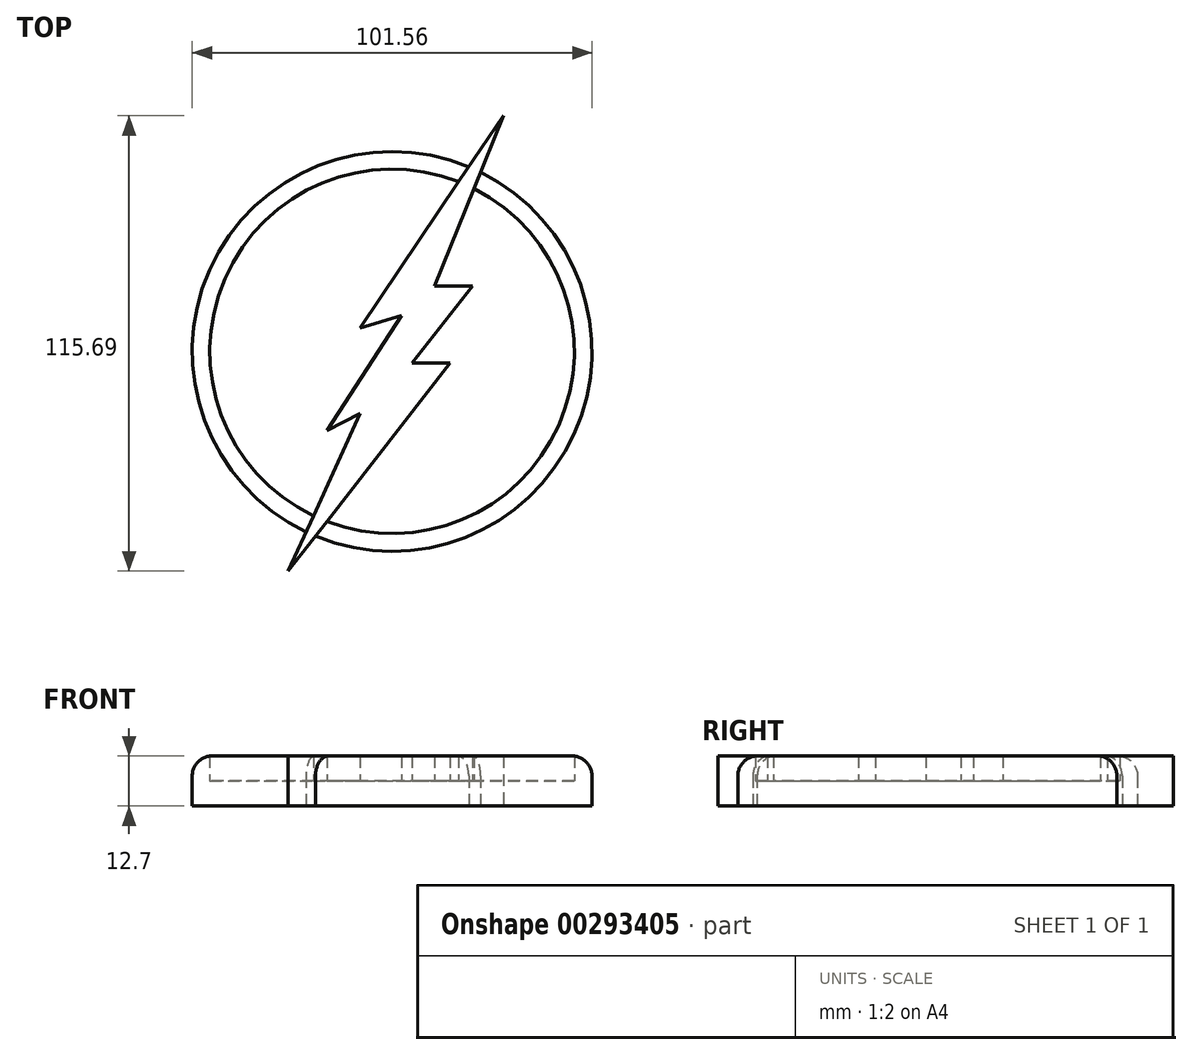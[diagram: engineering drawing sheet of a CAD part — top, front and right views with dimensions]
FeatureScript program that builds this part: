
annotation { "Feature Type Name" : "Feature", "Feature Type Description" : "" }
export const myFeature = defineFeature(function(context is Context, id is Id, definition is map)
    precondition{}
    {
        {
            var Q0;
            Q0=qCreatedBy(makeId("Top.planeOp"),FACE);
            var sketch = newSketch(context, id + "F0", { "sketchPlane" : qUnion([Q0])});
            skCircle(sketch, "E0", {"center": v(0, 0) * mm, "radius": 50.78 * mm});
            skCircle(sketch, "E1", {"center": v(0, 0) * mm, "radius": 46.3 * mm});
            skSolve(sketch);
        }
        {
            var Q0;
            Q0=makeQuery(id+"F0.imprint","IMPRINT",FACE,{"disambiguationData":[TD([[makeQuery(id+"F0.imprint","IMPRINT",EDGE,{"derivedFrom":sQuery(id+"F0.wireOp",EDGE,"E1")}),1.0]])]});
            extrude(context, id + "F1", {"entities" : qUnion([Q0]), "depth" : 6.35 * mm});
        }
        {
            var Q0;
            Q0=qSketchRegion(id+"F0",true);
            extrude(context, id + "F2", {"entities" : qUnion([Q0]), "operationType" : NewBodyOperationType.ADD, "depth" : 12.7 * mm});
        }
        {
            var Q0;
            Q0=makeQuery(id+"F2.opExtrude","CAP_EDGE",EDGE,{"disambiguationData":[OSD([sQuery(id+"F0.wireOp",EDGE,"E0")])],"isStart":false});
            fillet(context, id + "F3", {"entities" : qUnion([Q0]), "radius" : 5.08 * mm, "tangentPropagation" : true, "allowEdgeOverflow" : false});
        }
        {
            var Q0;
            Q0=makeQuery(id+"F1.opExtrude","CAP_FACE",FACE,{"disambiguationData":[OSD([sQuery(id+"F0.wireOp",EDGE,"E1")])],"isStart":false});
            var sketch = newSketch(context, id + "F4", { "sketchPlane" : qUnion([Q0])});
            skLineSegment(sketch, "E2", {"start": v(-26.37, -55.83) * mm, "end": v(14.74, -3) * mm});
            skLineSegment(sketch, "E3", {"start": v(14.74, -3) * mm, "end": v(5.11, -3) * mm});
            skLineSegment(sketch, "E4", {"start": v(5.11, -3) * mm, "end": v(20.4, 16.65) * mm});
            skLineSegment(sketch, "E5", {"start": v(20.4, 16.65) * mm, "end": v(10.83, 16.65) * mm});
            skLineSegment(sketch, "E6", {"start": v(10.83, 16.65) * mm, "end": v(28.27, 59.86) * mm});
            skLineSegment(sketch, "E7", {"start": v(-26.37, -55.83) * mm, "end": v(-8.18, -15.8) * mm});
            skLineSegment(sketch, "E8", {"start": v(-8.18, -15.8) * mm, "end": v(-16.54, -20.15) * mm});
            skLineSegment(sketch, "E9", {"start": v(-16.54, -20.15) * mm, "end": v(2.4, 9.1) * mm});
            skLineSegment(sketch, "E10", {"start": v(-8.18, 5.94) * mm, "end": v(28.27, 59.86) * mm});
            skLineSegment(sketch, "E11", {"start": v(-8.18, 5.94) * mm, "end": v(2.4, 9.1) * mm});
            skSolve(sketch);
        }
        {
            var Q0;
            Q0=qSketchRegion(id+"F4",true);
            extrude(context, id + "F5", {"entities" : qUnion([Q0]), "operationType" : NewBodyOperationType.ADD, "depth" : 6.35 * mm});
        }
        {
            var Q0;
            Q0=makeQuery(id+"F5.opExtrude","CAP_FACE",FACE,{"disambiguationData":[OSD([sQuery(id+"F4.wireOp",EDGE,"E2"),sQuery(id+"F4.wireOp",EDGE,"E3"),sQuery(id+"F4.wireOp",EDGE,"E4"),sQuery(id+"F4.wireOp",EDGE,"E5"),sQuery(id+"F4.wireOp",EDGE,"E6"),sQuery(id+"F4.wireOp",EDGE,"E7"),sQuery(id+"F4.wireOp",EDGE,"E8"),sQuery(id+"F4.wireOp",EDGE,"E9"),sQuery(id+"F4.wireOp",EDGE,"E10"),sQuery(id+"F4.wireOp",EDGE,"E11")])],"isStart":false});
            extrude(context, id + "F6", {"entities" : qUnion([Q0]), "operationType" : NewBodyOperationType.ADD, "oppositeDirection" : true, "depth" : 12.7 * mm});
        }
    });
